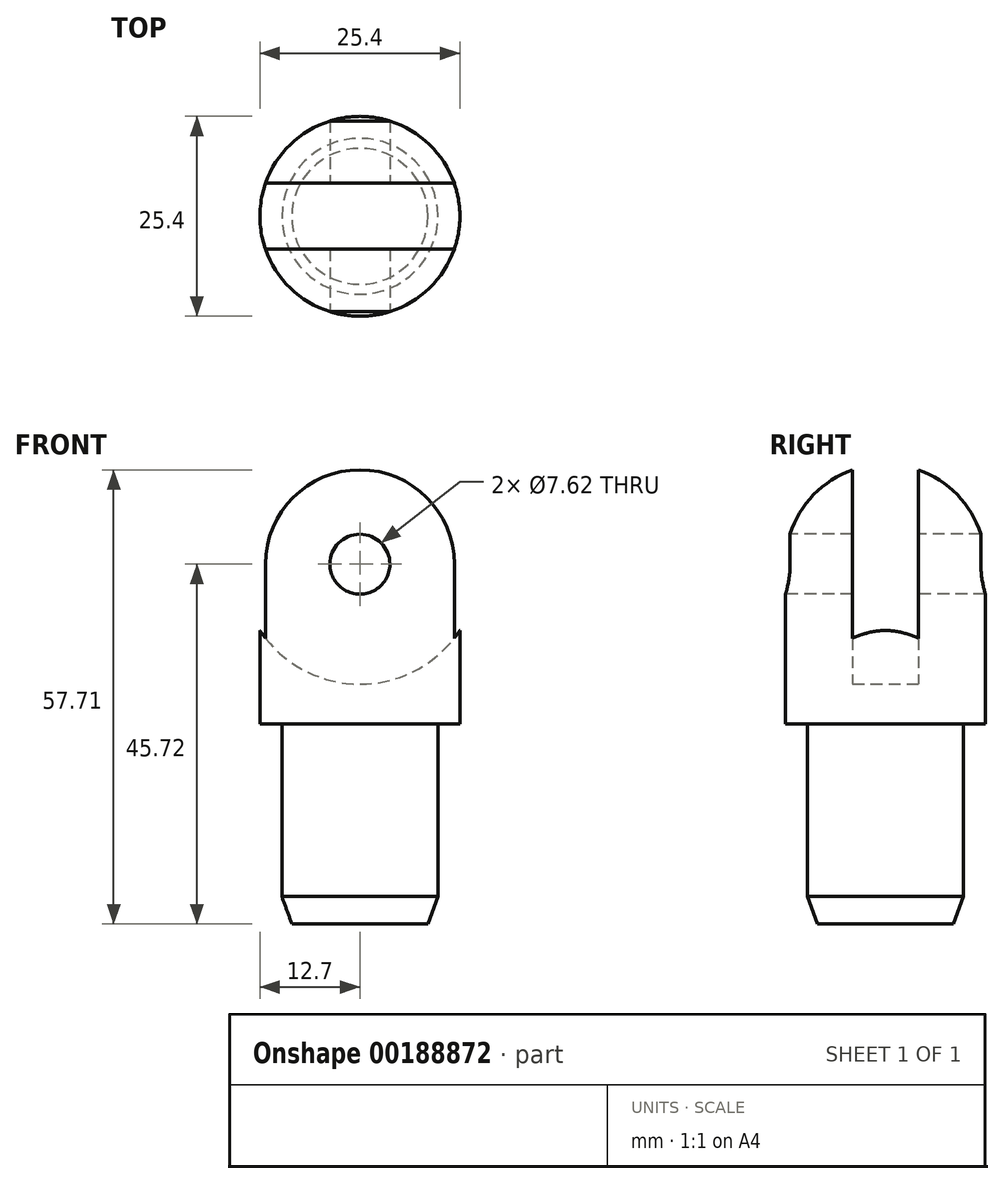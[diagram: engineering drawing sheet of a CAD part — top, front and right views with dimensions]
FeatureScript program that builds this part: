
annotation { "Feature Type Name" : "Feature", "Feature Type Description" : "" }
export const myFeature = defineFeature(function(context is Context, id is Id, definition is map)
    precondition{}
    {
        {
            var Q0;
            Q0=qCreatedBy(makeId("Top.planeOp"),FACE);
            var sketch = newSketch(context, id + "F0", { "sketchPlane" : qUnion([Q0])});
            skCircle(sketch, "E0", {"center": v(0, 0) * mm, "radius": 12.7 * mm});
            skSolve(sketch);
        }
        {
            var Q0;
            Q0=makeQuery(id+"F0.imprint","IMPRINT",FACE,{"disambiguationData":[TD([[makeQuery(id+"F0.imprint","IMPRINT",EDGE,{"derivedFrom":sQuery(id+"F0.wireOp",EDGE,"E0")}),1.0]])]});
            extrude(context, id + "F1", {"entities" : qUnion([Q0]), "oppositeDirection" : true, "depth" : 20.32 * mm});
        }
        {
            var Q0;
            Q0=qCreatedBy(makeId("Front.planeOp"),FACE);
            var sketch = newSketch(context, id + "F2", { "sketchPlane" : qUnion([Q0])});
            skCircle(sketch, "E1", {"center": v(0, 0) * mm, "radius": 15.24 * mm});
            skSolve(sketch);
        }
        {
            var Q0;
            Q0=qCreatedBy(makeId("Front.planeOp"),FACE);
            var sketch = newSketch(context, id + "F3", { "sketchPlane" : qUnion([Q0])});
            skLineSegment(sketch, "E2", {"start": v(0, 0) * mm, "end": v(0, 12.7) * mm});
            skLineSegment(sketch, "E3", {"start": v(12.7, -7.95) * mm, "end": v(12.7, -25.4) * mm});
            skLineSegment(sketch, "E4", {"start": v(12.7, -7.95) * mm, "end": v(12.7, 0) * mm, "construction": true});
            skLineSegment(sketch, "E5", {"start": v(0, 0) * mm, "end": v(12.7, 0) * mm});
            skArc(sketch, "E6", {"start": v(12.7, 0) * mm, "mid": v(8.98, 8.98) * mm, "end": v(0, 12.7) * mm});
            skLineSegment(sketch, "E7", {"start": v(0, 13.73) * mm, "end": v(0, 0) * mm, "construction": true});
            skSolve(sketch);
        }
        {
            var Q0;
            Q0 = qSketchRegion(id + "F3", true);
            var Q1;
            Q1=sQuery(id+"F3.wireOp",EDGE,"E7");
            revolve(context, id + "F4", {"operationType" : NewBodyOperationType.ADD, "entities" : qUnion([Q0]), "axis" : qUnion([Q1]), "revolveType" : RevolveType.FULL});
        }
        {
            var Q0;
            Q0 = qSketchRegion(id + "F2", true);
            extrude(context, id + "F5", {"entities" : qUnion([Q0]), "operationType" : NewBodyOperationType.REMOVE, "endBound" : BoundingType.SYMMETRIC, "depth" : 8.38 * mm});
        }
        {
            var Q0;
            Q0=makeQuery(id+"F5.boolean.opBoolean","COPY",FACE,{"derivedFrom":makeQuery(id+"F5.opExtrude","CAP_FACE",FACE,{"disambiguationData":[OSD([sQuery(id+"F2.wireOp",EDGE,"E1")])],"isStart":false})});
            var sketch = newSketch(context, id + "F6", { "sketchPlane" : qUnion([Q0])});
            skCircle(sketch, "E8", {"center": v(0, 0) * mm, "radius": 3.81 * mm});
            skSolve(sketch);
        }
        {
            var Q0;
            Q0 = qSketchRegion(id + "F6", true);
            extrude(context, id + "F7", {"entities" : qUnion([Q0]), "operationType" : NewBodyOperationType.REMOVE, "endBound" : BoundingType.SYMMETRIC, "depth" : 127 * mm});
        }
        {
            var Q0;
            Q0=makeQuery(id+"F1.opExtrude","CAP_FACE",FACE,{"disambiguationData":[OSD([sQuery(id+"F0.wireOp",EDGE,"E0")])],"isStart":false});
            var sketch = newSketch(context, id + "F8", { "sketchPlane" : qUnion([Q0])});
            skCircle(sketch, "E9", {"center": v(0, 0) * mm, "radius": 9.9 * mm});
            skSolve(sketch);
        }
        {
            var Q0;
            Q0 = qSketchRegion(id + "F8", true);
            extrude(context, id + "F9", {"entities" : qUnion([Q0]), "operationType" : NewBodyOperationType.ADD, "depth" : 25.4 * mm});
        }
        {
            var Q0;
            Q0=makeQuery(id+"F9.opExtrude","CAP_EDGE",EDGE,{"disambiguationData":[OSD([sQuery(id+"F8.wireOp",EDGE,"E9")])],"isStart":false});
            chamfer(context, id + "F10", {"entities" : qUnion([Q0]), "chamferType" : ChamferType.OFFSET_ANGLE, "width" : 1.27 * mm, "oppositeDirection" : false, "angle" : 70 * degree, "tangentPropagation" : true});
        }
    });
